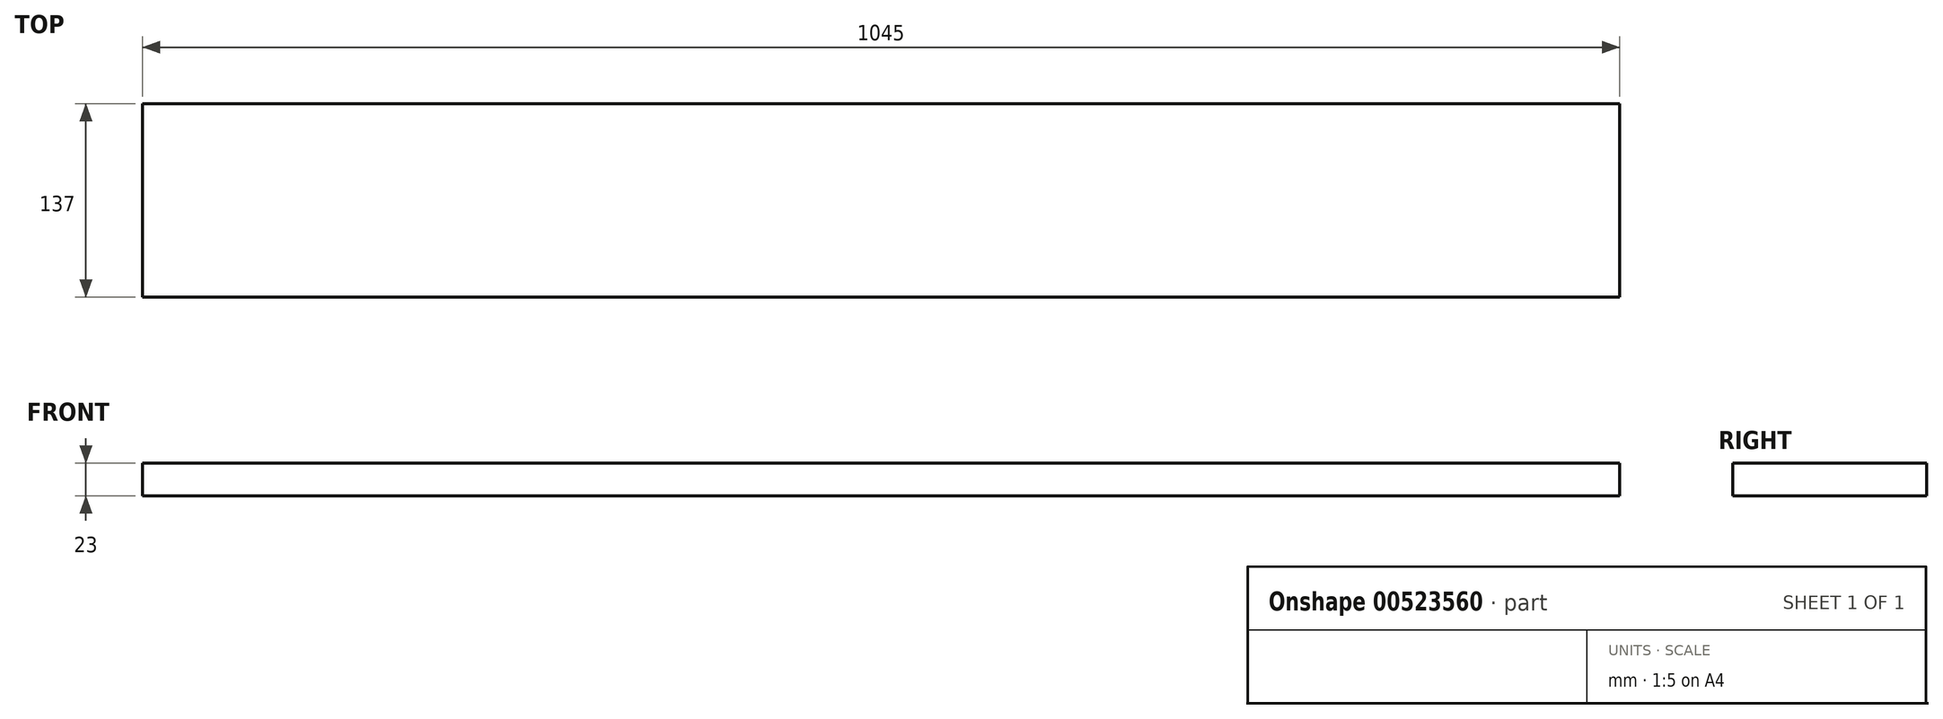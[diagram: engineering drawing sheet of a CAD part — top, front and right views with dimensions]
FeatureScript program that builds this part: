
annotation { "Feature Type Name" : "Feature", "Feature Type Description" : "" }
export const myFeature = defineFeature(function(context is Context, id is Id, definition is map)
    precondition{}
    {
        {
            var Q0;
            Q0=qCreatedBy(makeId("Top.planeOp"),FACE);
            var sketch = newSketch(context, id + "F0", { "sketchPlane" : qUnion([Q0])});
            skLineSegment(sketch, "E0.bottom", {"start": v(522.5, -68.5) * mm, "end": v(-522.5, -68.5) * mm});
            skLineSegment(sketch, "E0.top", {"start": v(522.5, 68.5) * mm, "end": v(-522.5, 68.5) * mm});
            skLineSegment(sketch, "E0.left", {"start": v(522.5, -68.5) * mm, "end": v(522.5, 68.5) * mm});
            skLineSegment(sketch, "E0.right", {"start": v(-522.5, -68.5) * mm, "end": v(-522.5, 68.5) * mm});
            skPoint(sketch, "E0.middle", {"position": v(0, 0) * mm});
            skSolve(sketch);
        }
        {
            var Q0;
            Q0 = qSketchRegion(id + "F0", true);
            extrude(context, id + "F1", {"entities" : qUnion([Q0]), "depth" : 23 * mm, "offsetDistance" : 25 * mm});
        }
    });
